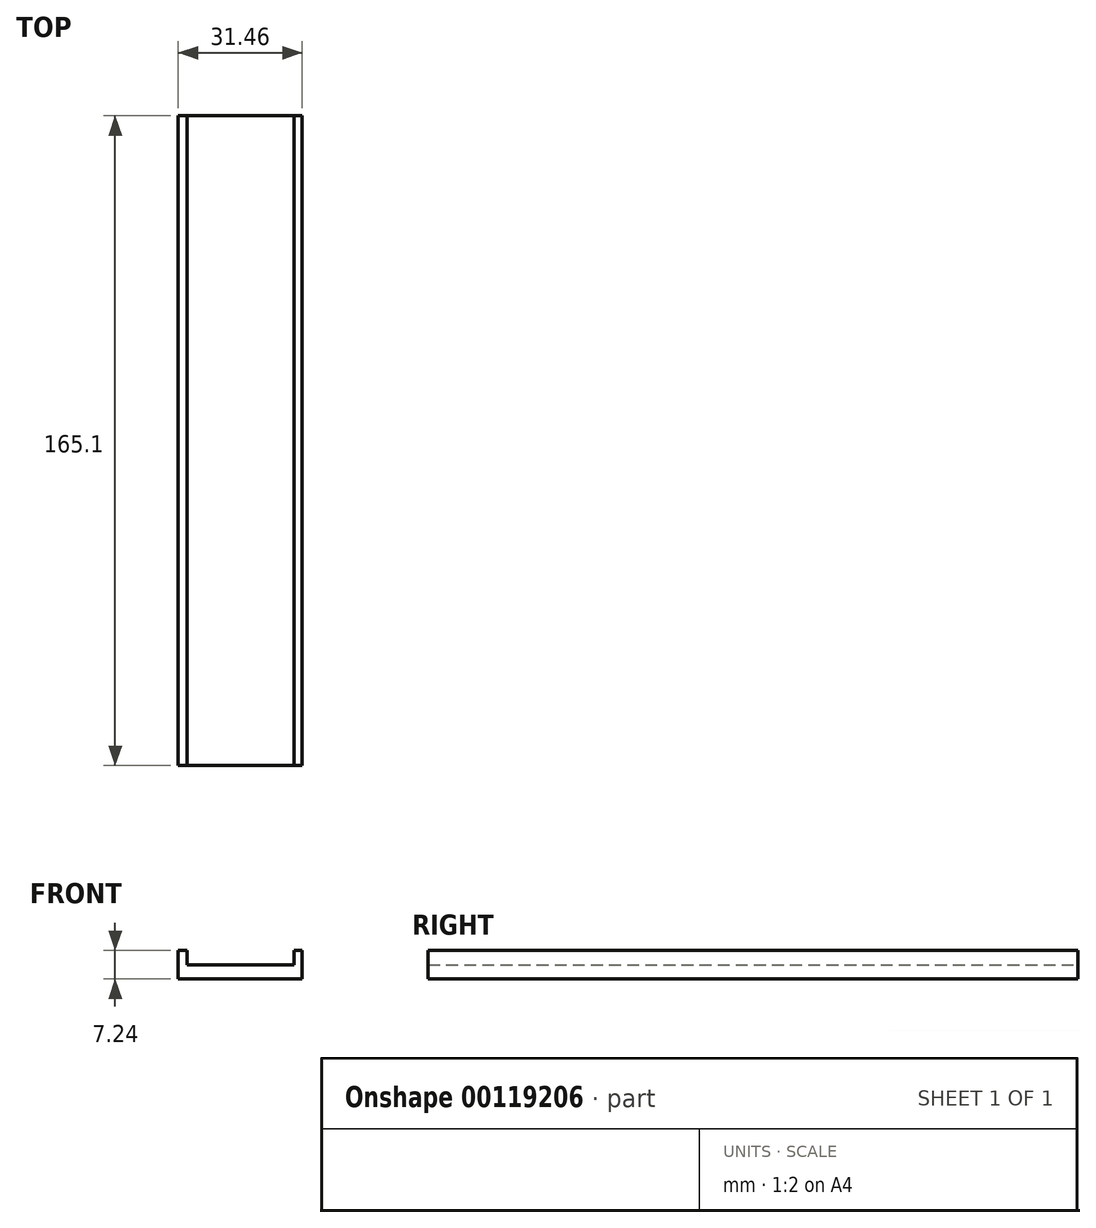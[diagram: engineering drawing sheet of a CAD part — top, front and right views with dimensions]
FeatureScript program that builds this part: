
annotation { "Feature Type Name" : "Feature", "Feature Type Description" : "" }
export const myFeature = defineFeature(function(context is Context, id is Id, definition is map)
    precondition{}
    {
        {
            var Q0;
            Q0=qCreatedBy(makeId("Front.planeOp"),FACE);
            var sketch = newSketch(context, id + "F0", { "sketchPlane" : qUnion([Q0])});
            skLineSegment(sketch, "E0.bottom", {"start": v(-15.73, -3.62) * mm, "end": v(15.73, -3.62) * mm});
            skLineSegment(sketch, "E0.top", {"start": v(-15.73, 3.62) * mm, "end": v(15.73, 3.62) * mm});
            skLineSegment(sketch, "E0.left", {"start": v(-15.73, -3.62) * mm, "end": v(-15.73, 3.62) * mm});
            skLineSegment(sketch, "E0.right", {"start": v(15.73, -3.62) * mm, "end": v(15.73, 3.62) * mm});
            skPoint(sketch, "E0.middle", {"position": v(0, 0) * mm});
            skSolve(sketch);
        }
        {
            var Q0;
            Q0=makeQuery(id+"F0.imprint","IMPRINT",FACE,{"disambiguationData":[TD([[makeQuery(id+"F0.imprint","IMPRINT",EDGE,{"derivedFrom":sQuery(id+"F0.wireOp",EDGE,"E0.bottom")}),1.0]])]});
            extrude(context, id + "F1", {"entities" : qUnion([Q0]), "depth" : 165.1 * mm});
        }
        {
            var Q0;
            Q0=makeQuery(id+"F1.opExtrude","CAP_FACE",FACE,{"disambiguationData":[OSD([sQuery(id+"F0.wireOp",EDGE,"E0.bottom"),sQuery(id+"F0.wireOp",EDGE,"E0.top"),sQuery(id+"F0.wireOp",EDGE,"E0.left"),sQuery(id+"F0.wireOp",EDGE,"E0.right")])],"isStart":true});
            var sketch = newSketch(context, id + "F2", { "sketchPlane" : qUnion([Q0])});
            skPoint(sketch, "E1.oppositeSnap0", {"position": v(15.73, 0) * mm});
            skLineSegment(sketch, "E1.bottom", {"start": v(-13.68, 3.62) * mm, "end": v(13.53, 3.62) * mm});
            skLineSegment(sketch, "E1.top", {"start": v(-13.68, 0) * mm, "end": v(13.53, 0) * mm});
            skLineSegment(sketch, "E1.left", {"start": v(-13.68, 3.62) * mm, "end": v(-13.68, 0) * mm});
            skLineSegment(sketch, "E1.right", {"start": v(13.53, 3.62) * mm, "end": v(13.53, 0) * mm});
            skSolve(sketch);
        }
        {
            var Q0;
            Q0=makeQuery(id+"F2.imprint","IMPRINT",FACE,{"disambiguationData":[TD([[makeQuery(id+"F2.imprint","IMPRINT",EDGE,{"derivedFrom":sQuery(id+"F2.wireOp",EDGE,"E1.bottom")}),1.0]])]});
            extrude(context, id + "F3", {"entities" : qUnion([Q0]), "operationType" : NewBodyOperationType.REMOVE, "oppositeDirection" : true, "depth" : 165.1 * mm});
        }
    });
